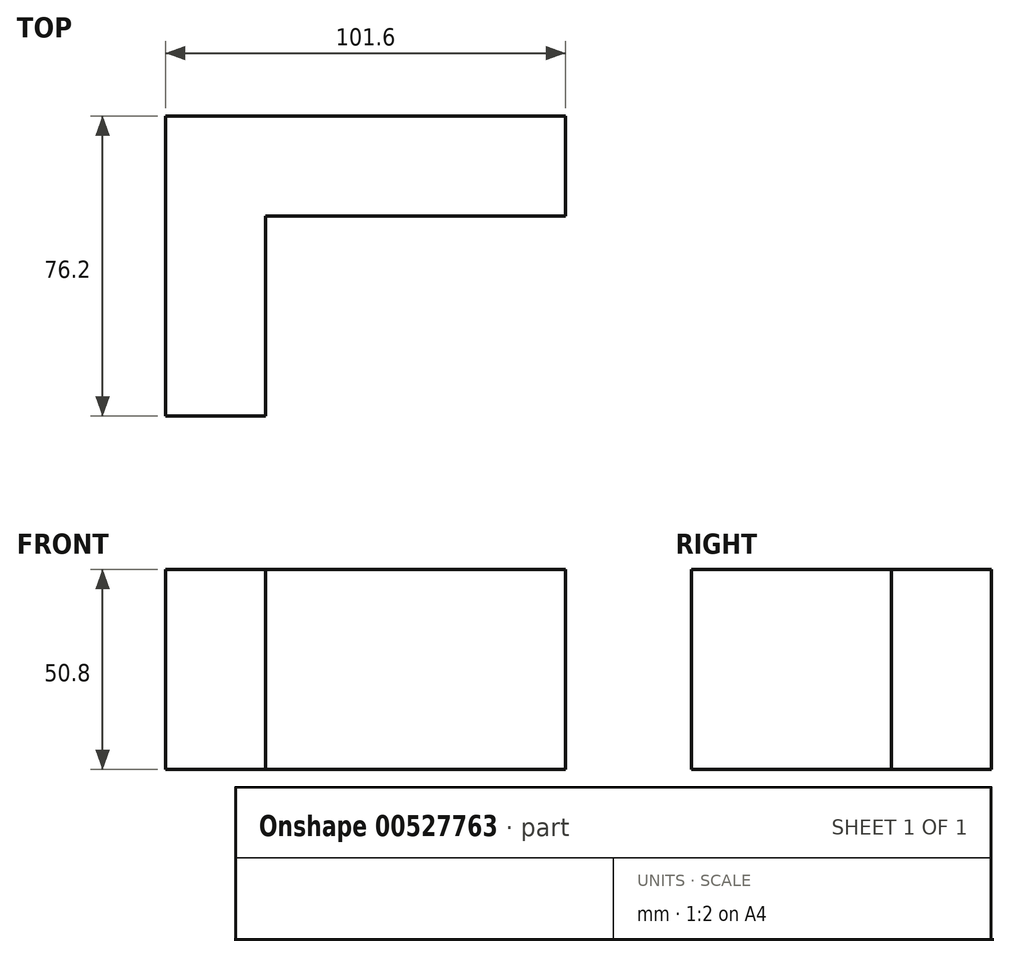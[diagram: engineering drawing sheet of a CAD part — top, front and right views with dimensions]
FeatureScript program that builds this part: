
annotation { "Feature Type Name" : "Feature", "Feature Type Description" : "" }
export const myFeature = defineFeature(function(context is Context, id is Id, definition is map)
    precondition{}
    {
        {
            var Q0;
            Q0=qCreatedBy(makeId("Top.planeOp"),FACE);
            var sketch = newSketch(context, id + "F0", { "sketchPlane" : qUnion([Q0])});
            skLineSegment(sketch, "E0", {"start": v(-76.5, -50.8) * mm, "end": v(-76.5, 25.4) * mm});
            skLineSegment(sketch, "E1", {"start": v(-76.5, 25.4) * mm, "end": v(75.9, 25.4) * mm});
            skLineSegment(sketch, "E2", {"start": v(75.9, 25.4) * mm, "end": v(75.9, 0) * mm});
            skLineSegment(sketch, "E3", {"start": v(75.9, 0) * mm, "end": v(-51.1, 0) * mm});
            skLineSegment(sketch, "E4", {"start": v(-51.1, 0) * mm, "end": v(-51.1, -50.8) * mm});
            skLineSegment(sketch, "E5", {"start": v(-51.1, -50.8) * mm, "end": v(-76.5, -50.8) * mm});
            skLineSegment(sketch, "E6.bottom", {"start": v(25.1, 25.4) * mm, "end": v(75.9, 25.4) * mm});
            skLineSegment(sketch, "E6.top", {"start": v(25.1, 0) * mm, "end": v(75.9, 0) * mm});
            skLineSegment(sketch, "E6.left", {"start": v(25.1, 25.4) * mm, "end": v(25.1, 0) * mm});
            skSolve(sketch);
        }
        {
            var Q0;
            Q0=makeQuery(id+"F0.imprint","IMPRINT",FACE,{"disambiguationData":[TD([[makeQuery(id+"F0.imprint","IMPRINT",EDGE,{"derivedFrom":sQuery(id+"F0.wireOp",EDGE,"E0")}),-1.0]])]});
            extrude(context, id + "F1", {"entities" : qUnion([Q0]), "depth" : 50.8 * mm, "offsetDistance" : 25.4 * mm});
        }
    });
